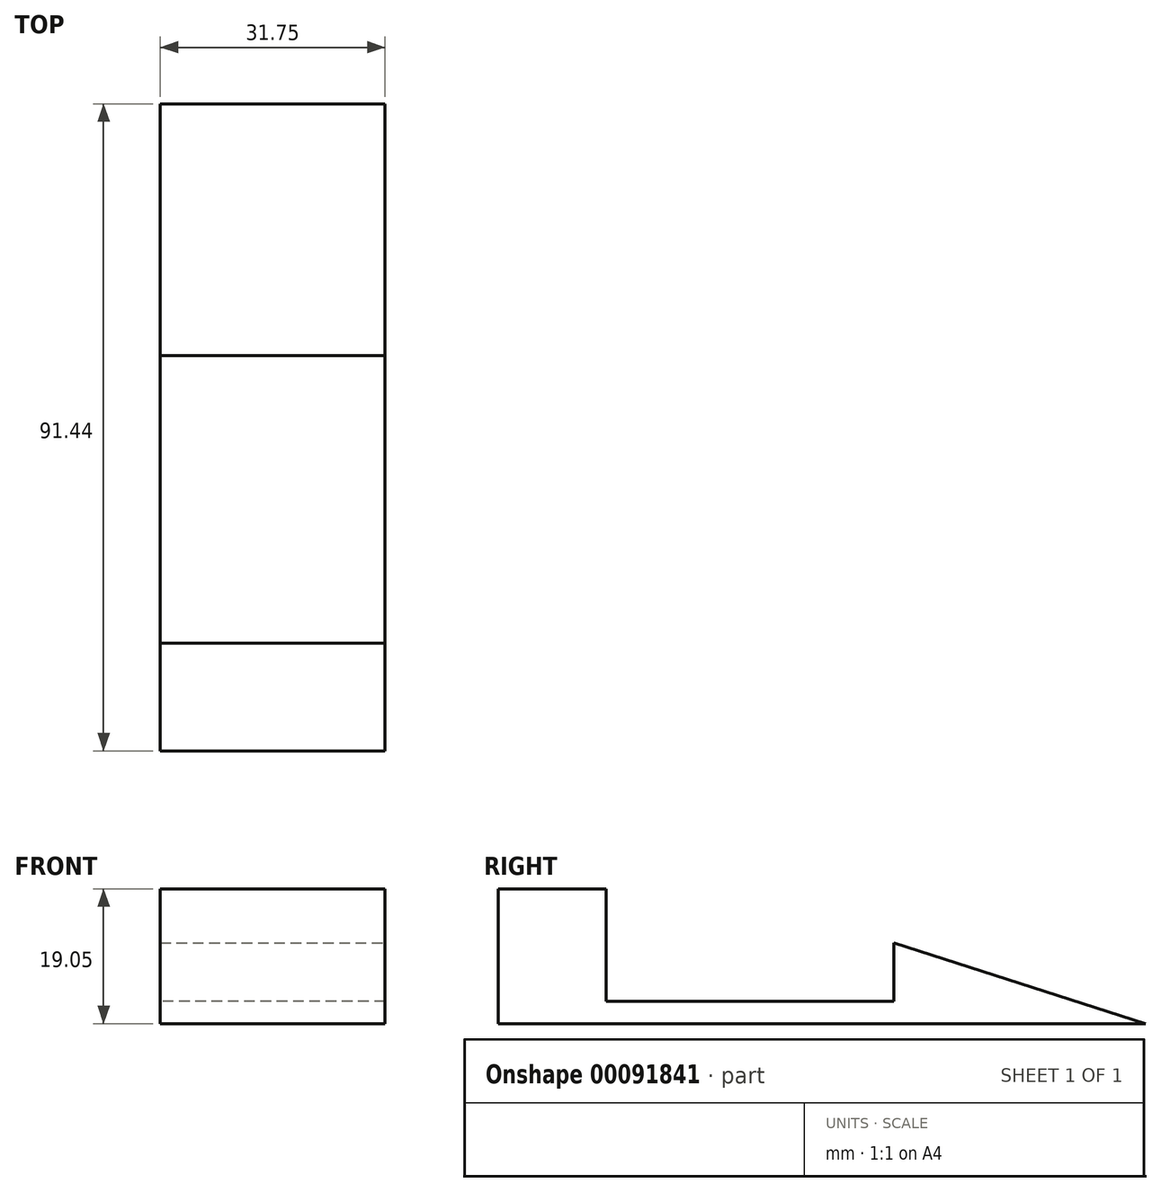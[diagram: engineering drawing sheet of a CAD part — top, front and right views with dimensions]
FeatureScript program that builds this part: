
annotation { "Feature Type Name" : "Feature", "Feature Type Description" : "" }
export const myFeature = defineFeature(function(context is Context, id is Id, definition is map)
    precondition{}
    {
        {
            var Q0;
            Q0=qCreatedBy(makeId("Top.planeOp"),FACE);
            var sketch = newSketch(context, id + "F0", { "sketchPlane" : qUnion([Q0])});
            skLineSegment(sketch, "E0.bottom", {"start": v(0, 0) * mm, "end": v(-31.75, 0) * mm});
            skLineSegment(sketch, "E0.top", {"start": v(0, 91.44) * mm, "end": v(-31.75, 91.44) * mm});
            skLineSegment(sketch, "E0.left", {"start": v(0, 0) * mm, "end": v(0, 91.44) * mm});
            skLineSegment(sketch, "E0.right", {"start": v(-31.75, 0) * mm, "end": v(-31.75, 91.44) * mm});
            skLineSegment(sketch, "E1", {"start": v(-31.75, 0) * mm, "end": v(-31.75, 15.24) * mm});
            skLineSegment(sketch, "E2", {"start": v(-31.75, 15.24) * mm, "end": v(0, 15.24) * mm});
            skLineSegment(sketch, "E3", {"start": v(-31.75, 91.44) * mm, "end": v(-31.75, 55.88) * mm});
            skLineSegment(sketch, "E4", {"start": v(-31.75, 55.88) * mm, "end": v(0, 55.88) * mm});
            skSolve(sketch);
        }
        {
            var Q0;
            Q0=makeQuery(id+"F0.imprint","IMPRINT",FACE,{"disambiguationData":[TD([[makeQuery(id+"F0.imprint","IMPRINT",EDGE,{"derivedFrom":sQuery(id+"F0.wireOp",EDGE,"E0.right")}),-1.0]])]});
            extrude(context, id + "F1", {"entities" : qUnion([Q0]), "depth" : 3.17 * mm});
        }
        {
            var Q0;
            {var subQ0=sQuery(id+"F0.wireOp",EDGE,"E0.bottom");Q0=makeQuery(id+"F0.imprint","IMPRINT",FACE,{"disambiguationData":[TD([[makeQuery(id+"F0.imprint","IMPRINT",EDGE,{"derivedFrom":subQ0}),-1.0]])]});}
            extrude(context, id + "F2", {"entities" : qUnion([Q0]), "operationType" : NewBodyOperationType.ADD, "depth" : 19.05 * mm});
        }
        {
            var Q0;
            {var subQ0=sQuery(id+"F0.wireOp",EDGE,"E0.top");Q0=makeQuery(id+"F0.imprint","IMPRINT",FACE,{"disambiguationData":[TD([[makeQuery(id+"F0.imprint","IMPRINT",EDGE,{"derivedFrom":subQ0}),1.0]])]});}
            extrude(context, id + "F3", {"entities" : qUnion([Q0]), "operationType" : NewBodyOperationType.ADD, "depth" : 11.43 * mm});
        }
        {
            var Q0;
            {var subQ0=sQuery(id+"F0.wireOp",EDGE,"E0.left");Q0=makeQuery(id+"F3.boolean.opBoolean","MERGE",FACE,{"derivedFrom":[makeQuery(id+"F2.boolean.opBoolean","MERGE",FACE,{"derivedFrom":[makeQuery(id+"F1.opExtrude","SWEPT_FACE",FACE,{"disambiguationData":[OSD([subQ0])]}),makeQuery(id+"F2.opExtrude","SWEPT_FACE",FACE,{"disambiguationData":[OSD([subQ0])]})]}),makeQuery(id+"F3.opExtrude","SWEPT_FACE",FACE,{"disambiguationData":[OSD([subQ0])]})]});}
            var sketch = newSketch(context, id + "F4", { "sketchPlane" : qUnion([Q0])});
            skPoint(sketch, "E5.0", {"position": v(55.88, 11.43) * mm});
            skPoint(sketch, "E6.0", {"position": v(91.44, 0) * mm});
            skLineSegment(sketch, "E7", {"start": v(55.88, 11.43) * mm, "end": v(91.44, 0) * mm});
            skLineSegment(sketch, "E8", {"start": v(91.44, 11.43) * mm, "end": v(91.44, 0) * mm});
            skLineSegment(sketch, "E9", {"start": v(55.88, 11.43) * mm, "end": v(91.44, 11.43) * mm});
            skSolve(sketch);
        }
        {
            var Q0;
            Q0=makeQuery(id+"F4.imprint","IMPRINT",FACE,{"disambiguationData":[TD([[makeQuery(id+"F4.imprint","IMPRINT",EDGE,{"derivedFrom":sQuery(id+"F4.wireOp",EDGE,"E7")}),1.0]])]});
            var Q1;
            Q1=makeQuery(id+"F3.boolean.opBoolean","MERGE",FACE,{"derivedFrom":[makeQuery(id+"F2.boolean.opBoolean","MERGE",FACE,{"derivedFrom":[makeQuery(id+"F1.opExtrude","SWEPT_FACE",FACE,{"disambiguationData":[OSD([sQuery(id+"F0.wireOp",EDGE,"E0.right")])]}),makeQuery(id+"F2.opExtrude","SWEPT_FACE",FACE,{"disambiguationData":[OSD([sQuery(id+"F0.wireOp",EDGE,"E1")])]})]}),makeQuery(id+"F3.opExtrude","SWEPT_FACE",FACE,{"disambiguationData":[OSD([sQuery(id+"F0.wireOp",EDGE,"E3")])]})]});
            extrude(context, id + "F5", {"entities" : qUnion([Q0]), "operationType" : NewBodyOperationType.REMOVE, "endBound" : BoundingType.UP_TO_SURFACE, "oppositeDirection" : true, "endBoundEntityFace" : qUnion([Q1]), "depth" : 25.4 * mm});
        }
    });
